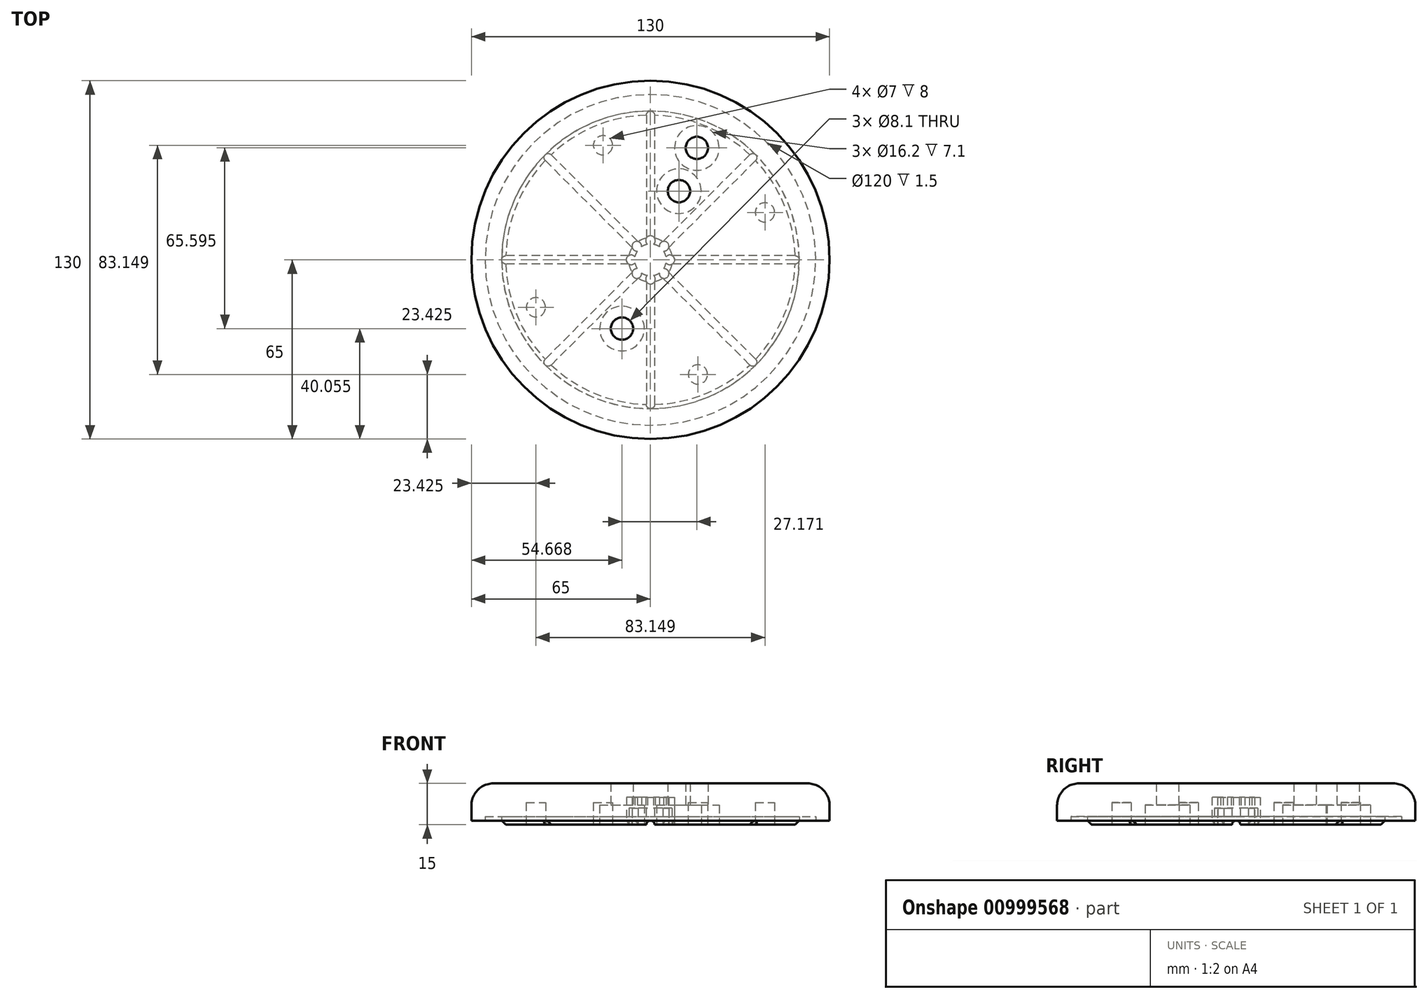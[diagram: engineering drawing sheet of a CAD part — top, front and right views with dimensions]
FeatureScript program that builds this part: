
annotation { "Feature Type Name" : "Feature", "Feature Type Description" : "" }
export const myFeature = defineFeature(function(context is Context, id is Id, definition is map)
    precondition{}
    {
        {
            var Q0;
            Q0=qCreatedBy(makeId("Top.planeOp"),FACE);
            var sketch = newSketch(context, id + "F0", { "sketchPlane" : qUnion([Q0])});
            skCircle(sketch, "E0", {"center": v(0, 0) * mm, "radius": 65 * mm});
            skSolve(sketch);
        }
        {
            var Q0;
            Q0 = qSketchRegion(id + "F0", true);
            extrude(context, id + "F1", {"entities" : qUnion([Q0]), "depth" : 15 * mm, "offsetDistance" : 25.4 * mm});
        }
        {
            var Q0;
            Q0=makeQuery(id+"F1.opExtrude","CAP_FACE",FACE,{"disambiguationData":[OSD([sQuery(id+"F0.wireOp",EDGE,"E0")])],"isStart":false});
            fillet(context, id + "F2", {"entities" : qUnion([Q0]), "radius" : 8 * mm, "tangentPropagation" : true, "allowEdgeOverflow" : false});
        }
        {
            var Q0;
            Q0=makeQuery(id+"F1.opExtrude","CAP_FACE",FACE,{"disambiguationData":[OSD([sQuery(id+"F0.wireOp",EDGE,"E0")])],"isStart":true});
            var sketch = newSketch(context, id + "F3", { "sketchPlane" : qUnion([Q0])});
            skCircle(sketch, "E1", {"center": v(0, 0) * mm, "radius": 67.5 * mm});
            skCircle(sketch, "E2", {"center": v(0, 0) * mm, "radius": 54 * mm});
            skCircle(sketch, "E3", {"center": v(0, 0) * mm, "radius": 60 * mm});
            skSolve(sketch);
        }
        {
            var Q0;
            Q0=makeQuery(id+"F3.imprint","IMPRINT",FACE,{"disambiguationData":[TD([[makeQuery(id+"F3.imprint","IMPRINT",EDGE,{"derivedFrom":sQuery(id+"F3.wireOp",EDGE,"E2")}),-1.0]])]});
            extrude(context, id + "F4", {"entities" : qUnion([Q0]), "operationType" : NewBodyOperationType.REMOVE, "oppositeDirection" : true, "depth" : 3 * mm, "offsetDistance" : 25 * mm});
        }
        {
            var Q0;
            Q0=makeQuery(id+"F1.opExtrude","CAP_FACE",FACE,{"disambiguationData":[OSD([sQuery(id+"F0.wireOp",EDGE,"E0")])],"isStart":true});
            var sketch = newSketch(context, id + "F5", { "sketchPlane" : qUnion([Q0])});
            skCircle(sketch, "E4", {"center": v(0, 0) * mm, "radius": 8 * mm});
            skSolve(sketch);
        }
        {
            var Q0;
            Q0=makeQuery(id+"F5.imprint","IMPRINT",FACE,{"disambiguationData":[TD([[makeQuery(id+"F5.imprint","IMPRINT",EDGE,{"derivedFrom":sQuery(id+"F5.wireOp",EDGE,"E4")}),1.0]])]});
            extrude(context, id + "F6", {"entities" : qUnion([Q0]), "operationType" : NewBodyOperationType.REMOVE, "oppositeDirection" : true, "depth" : 10 * mm, "offsetDistance" : 25 * mm});
        }
        {
            var Q0;
            Q0=qCreatedBy(makeId("Front.planeOp"),FACE);
            var Q1;
            Q1=qCreatedBy(makeId("Right.planeOp"),FACE);
            cPlane(context, id + "F7", {"entities" : qUnion([Q0, Q1]), "cplaneType" : CPlaneType.MID_PLANE, "offset" : 25 * mm, "width" : 150 * mm, "height" : 150 * mm});
        }
        {
            var Q0;
            Q0=qCreatedBy(makeId("Front.planeOp"),FACE);
            var Q1;
            Q1=qCreatedBy(makeId("Right.planeOp"),FACE);
            cPlane(context, id + "F8", {"entities" : qUnion([Q0, Q1]), "cplaneType" : CPlaneType.MID_PLANE, "offset" : 25 * mm, "flipAlignment" : true, "width" : 150 * mm, "height" : 150 * mm});
        }
        {
            var Q0;
            Q0=qCreatedBy(makeId("Front.planeOp"),FACE);
            var sketch = newSketch(context, id + "F9", { "sketchPlane" : qUnion([Q0])});
            skCircle(sketch, "E5", {"center": v(0, 0) * mm, "radius": 1.5 * mm});
            skSolve(sketch);
        }
        {
            var Q0;
            Q0=makeQuery(id+"F9.imprint","IMPRINT",FACE,{"disambiguationData":[TD([[makeQuery(id+"F9.imprint","IMPRINT",EDGE,{"derivedFrom":sQuery(id+"F9.wireOp",EDGE,"E5")}),1.0]])]});
            var Q1;
            Q1=makeQuery(id+"F4.boolean.opBoolean","COPY",FACE,{"derivedFrom":makeQuery(id+"F4.opExtrude","SWEPT_FACE",FACE,{"disambiguationData":[OSD([sQuery(id+"F3.wireOp",EDGE,"E2")])]})});
            var Q2;
            Q2=makeQuery(id+"F4.boolean.opBoolean","COPY",FACE,{"derivedFrom":makeQuery(id+"F4.opExtrude","SWEPT_FACE",FACE,{"disambiguationData":[OSD([sQuery(id+"F3.wireOp",EDGE,"E2")])]})});
            extrude(context, id + "F10", {"entities" : qUnion([Q0]), "operationType" : NewBodyOperationType.REMOVE, "endBound" : BoundingType.UP_TO_SURFACE, "oppositeDirection" : true, "depth" : 25 * mm, "endBoundEntityFace" : qUnion([Q1]), "offsetDistance" : 25 * mm, "hasSecondDirection" : true, "secondDirectionBound" : SecondDirectionBoundingType.UP_TO_SURFACE, "secondDirectionOppositeDirection" : false, "secondDirectionDepth" : 25 * mm, "secondDirectionBoundEntityFace" : qUnion([Q2])});
        }
        {
            var Q0;
            Q0=qCreatedBy(makeId("Right.planeOp"),FACE);
            var sketch = newSketch(context, id + "F11", { "sketchPlane" : qUnion([Q0])});
            skCircle(sketch, "E6", {"center": v(0, 0) * mm, "radius": 1.5 * mm});
            skSolve(sketch);
        }
        {
            var Q0;
            Q0=makeQuery(id+"F11.imprint","IMPRINT",FACE,{"disambiguationData":[TD([[makeQuery(id+"F11.imprint","IMPRINT",EDGE,{"derivedFrom":sQuery(id+"F11.wireOp",EDGE,"E6")}),1.0]])]});
            var Q1;
            Q1=makeQuery(id+"F4.boolean.opBoolean","COPY",FACE,{"derivedFrom":makeQuery(id+"F4.opExtrude","SWEPT_FACE",FACE,{"disambiguationData":[OSD([sQuery(id+"F3.wireOp",EDGE,"E2")])]})});
            var Q2;
            Q2=makeQuery(id+"F4.boolean.opBoolean","COPY",FACE,{"derivedFrom":makeQuery(id+"F4.opExtrude","SWEPT_FACE",FACE,{"disambiguationData":[OSD([sQuery(id+"F3.wireOp",EDGE,"E2")])]})});
            extrude(context, id + "F12", {"entities" : qUnion([Q0]), "operationType" : NewBodyOperationType.REMOVE, "endBound" : BoundingType.UP_TO_SURFACE, "depth" : 25 * mm, "endBoundEntityFace" : qUnion([Q1]), "offsetDistance" : 25 * mm, "hasSecondDirection" : true, "secondDirectionBound" : SecondDirectionBoundingType.UP_TO_SURFACE, "secondDirectionOppositeDirection" : true, "secondDirectionDepth" : 25 * mm, "secondDirectionBoundEntityFace" : qUnion([Q2])});
        }
        {
            var Q0;
            Q0=qCreatedBy(id+"F7.planeOp",FACE);
            var sketch = newSketch(context, id + "F13", { "sketchPlane" : qUnion([Q0])});
            skCircle(sketch, "E7", {"center": v(0, 0) * mm, "radius": 1.5 * mm});
            skSolve(sketch);
        }
        {
            var Q0;
            Q0 = qSketchRegion(id + "F13", true);
            var Q1;
            Q1=makeQuery(id+"F4.boolean.opBoolean","COPY",FACE,{"derivedFrom":makeQuery(id+"F4.opExtrude","SWEPT_FACE",FACE,{"disambiguationData":[OSD([sQuery(id+"F3.wireOp",EDGE,"E2")])]})});
            var Q2;
            Q2=makeQuery(id+"F4.boolean.opBoolean","COPY",FACE,{"derivedFrom":makeQuery(id+"F4.opExtrude","SWEPT_FACE",FACE,{"disambiguationData":[OSD([sQuery(id+"F3.wireOp",EDGE,"E2")])]})});
            extrude(context, id + "F14", {"entities" : qUnion([Q0]), "operationType" : NewBodyOperationType.REMOVE, "endBound" : BoundingType.UP_TO_SURFACE, "oppositeDirection" : true, "depth" : 25 * mm, "endBoundEntityFace" : qUnion([Q1]), "offsetDistance" : 25 * mm, "hasSecondDirection" : true, "secondDirectionBound" : SecondDirectionBoundingType.UP_TO_SURFACE, "secondDirectionOppositeDirection" : false, "secondDirectionDepth" : 25 * mm, "secondDirectionBoundEntityFace" : qUnion([Q2])});
        }
        {
            var Q0;
            Q0=qCreatedBy(id+"F8.planeOp",FACE);
            var sketch = newSketch(context, id + "F15", { "sketchPlane" : qUnion([Q0])});
            skCircle(sketch, "E8", {"center": v(0, 0) * mm, "radius": 1.5 * mm});
            skSolve(sketch);
        }
        {
            var Q0;
            Q0 = qSketchRegion(id + "F15", true);
            var Q1;
            Q1=makeQuery(id+"F4.boolean.opBoolean","COPY",FACE,{"derivedFrom":makeQuery(id+"F4.opExtrude","SWEPT_FACE",FACE,{"disambiguationData":[OSD([sQuery(id+"F3.wireOp",EDGE,"E2")])]})});
            var Q2;
            Q2=makeQuery(id+"F4.boolean.opBoolean","COPY",FACE,{"derivedFrom":makeQuery(id+"F4.opExtrude","SWEPT_FACE",FACE,{"disambiguationData":[OSD([sQuery(id+"F3.wireOp",EDGE,"E2")])]})});
            extrude(context, id + "F16", {"entities" : qUnion([Q0]), "operationType" : NewBodyOperationType.REMOVE, "endBound" : BoundingType.UP_TO_SURFACE, "oppositeDirection" : true, "depth" : 25 * mm, "endBoundEntityFace" : qUnion([Q1]), "offsetDistance" : 25 * mm, "hasSecondDirection" : true, "secondDirectionBound" : SecondDirectionBoundingType.UP_TO_SURFACE, "secondDirectionOppositeDirection" : false, "secondDirectionDepth" : 25 * mm, "secondDirectionBoundEntityFace" : qUnion([Q2])});
        }
        {
            var Q0;
            Q0=makeQuery(id+"F6.boolean.opBoolean","COPY",FACE,{"derivedFrom":makeQuery(id+"F6.opExtrude","CAP_FACE",FACE,{"disambiguationData":[OSD([sQuery(id+"F5.wireOp",EDGE,"E4")])],"isStart":false})});
            var sketch = newSketch(context, id + "F17", { "sketchPlane" : qUnion([Q0])});
            skCircle(sketch, "E9.0", {"center": v(0, 0) * mm, "radius": 8 * mm});
            skCircle(sketch, "E10", {"center": v(0, 0) * mm, "radius": 5.75 * mm});
            skSolve(sketch);
        }
        {
            var Q0;
            Q0=makeQuery(id+"F17.imprint","IMPRINT",FACE,{"disambiguationData":[TD([[makeQuery(id+"F17.imprint","IMPRINT",EDGE,{"derivedFrom":sQuery(id+"F17.wireOp",EDGE,"E9.0")}),1.0]])]});
            extrude(context, id + "F18", {"entities" : qUnion([Q0]), "operationType" : NewBodyOperationType.ADD, "depth" : 4 * mm, "offsetDistance" : 25 * mm});
        }
        {
            var Q0;
            Q0=makeQuery(id+"F12.boolean.opBoolean","SPLIT",FACE,{"disambiguationData":[TD([makeQuery(id+"F10.boolean.opBoolean","COPY",FACE,{"disambiguationData":[OD(0.0)],"derivedFrom":makeQuery(id+"F10.opExtrude","SWEPT_FACE",FACE,{"disambiguationData":[OSD([sQuery(id+"F9.wireOp",EDGE,"E5")])]})})])],"derivedFrom":makeQuery(id+"F10.boolean.opBoolean","SPLIT",FACE,{"disambiguationData":[OD(0.0)],"derivedFrom":makeQuery(id+"F1.opExtrude","CAP_FACE",FACE,{"disambiguationData":[OSD([sQuery(id+"F0.wireOp",EDGE,"E0")])],"isStart":true})})});
            var sketch = newSketch(context, id + "F19", { "sketchPlane" : qUnion([Q0])});
            skCircle(sketch, "E11", {"center": v(0, 7) * mm, "radius": 1.75 * mm});
            skCircle(sketch, "E12.1.0", {"center": v(-4.95, 4.95) * mm, "radius": 1.75 * mm});
            skCircle(sketch, "E12.2.0", {"center": v(-7, 0) * mm, "radius": 1.75 * mm});
            skCircle(sketch, "E12.3.0", {"center": v(-4.95, -4.95) * mm, "radius": 1.75 * mm});
            skPoint(sketch, "E12.center", {"position": v(0, 0) * mm});
            skCircle(sketch, "E13.1.4.0", {"center": v(0, -7) * mm, "radius": 1.75 * mm});
            skCircle(sketch, "E13.1.5.0", {"center": v(4.95, -4.95) * mm, "radius": 1.75 * mm});
            skCircle(sketch, "E14.1.6.0", {"center": v(7, 0) * mm, "radius": 1.75 * mm});
            skCircle(sketch, "E14.1.7.0", {"center": v(4.95, 4.95) * mm, "radius": 1.75 * mm});
            skSolve(sketch);
        }
        {
            var Q0;
            Q0 = qSketchRegion(id + "F19", true);
            extrude(context, id + "F20", {"entities" : qUnion([Q0]), "operationType" : NewBodyOperationType.REMOVE, "oppositeDirection" : true, "depth" : 10 * mm, "offsetDistance" : 25 * mm});
        }
        {
            var Q0;
            {var subQ2=makeQuery(id+"F10.boolean.opBoolean","COPY",FACE,{"disambiguationData":[OD(0.0)],"derivedFrom":makeQuery(id+"F10.opExtrude","SWEPT_FACE",FACE,{"disambiguationData":[OSD([sQuery(id+"F9.wireOp",EDGE,"E5")])]})});Q0=makeQuery(id+"F14.boolean.opBoolean","SPLIT",FACE,{"disambiguationData":[TD([subQ2])],"derivedFrom":makeQuery(id+"F12.boolean.opBoolean","SPLIT",FACE,{"disambiguationData":[TD([subQ2])],"derivedFrom":makeQuery(id+"F10.boolean.opBoolean","SPLIT",FACE,{"disambiguationData":[OD(0.0)],"derivedFrom":makeQuery(id+"F1.opExtrude","CAP_FACE",FACE,{"disambiguationData":[OSD([sQuery(id+"F0.wireOp",EDGE,"E0")])],"isStart":true})})})});}
            var sketch = newSketch(context, id + "F21", { "sketchPlane" : qUnion([Q0])});
            skLineSegment(sketch, "E15", {"start": v(-20.66, 49.89) * mm, "end": v(0, 0) * mm, "construction": true});
            skLineSegment(sketch, "E16", {"start": v(0, 0) * mm, "end": v(20.66, -49.89) * mm, "construction": true});
            skCircle(sketch, "E17", {"center": v(-10.33, 24.94) * mm, "radius": 4.05 * mm});
            skCircle(sketch, "E18", {"center": v(10.33, -24.94) * mm, "radius": 4.05 * mm});
            skCircle(sketch, "E19", {"center": v(16.84, -40.65) * mm, "radius": 4.05 * mm});
            skSolve(sketch);
        }
        {
            var Q0;
            Q0 = qSketchRegion(id + "F21", true);
            extrude(context, id + "F22", {"entities" : qUnion([Q0]), "operationType" : NewBodyOperationType.REMOVE, "endBound" : BoundingType.THROUGH_ALL, "oppositeDirection" : true, "depth" : 25 * mm, "offsetDistance" : 25 * mm});
        }
        {
            var Q0;
            {var subQ2=makeQuery(id+"F10.boolean.opBoolean","COPY",FACE,{"disambiguationData":[OD(0.0)],"derivedFrom":makeQuery(id+"F10.opExtrude","SWEPT_FACE",FACE,{"disambiguationData":[OSD([sQuery(id+"F9.wireOp",EDGE,"E5")])]})});Q0=makeQuery(id+"F14.boolean.opBoolean","SPLIT",FACE,{"disambiguationData":[TD([subQ2])],"derivedFrom":makeQuery(id+"F12.boolean.opBoolean","SPLIT",FACE,{"disambiguationData":[TD([subQ2])],"derivedFrom":makeQuery(id+"F10.boolean.opBoolean","SPLIT",FACE,{"disambiguationData":[OD(0.0)],"derivedFrom":makeQuery(id+"F1.opExtrude","CAP_FACE",FACE,{"disambiguationData":[OSD([sQuery(id+"F0.wireOp",EDGE,"E0")])],"isStart":true})})})});}
            var sketch = newSketch(context, id + "F23", { "sketchPlane" : qUnion([Q0])});
            skCircle(sketch, "E20", {"center": v(-10.33, 24.94) * mm, "radius": 8.1 * mm});
            skCircle(sketch, "E21", {"center": v(10.33, -24.94) * mm, "radius": 8.1 * mm});
            skCircle(sketch, "E22", {"center": v(16.84, -40.65) * mm, "radius": 8.1 * mm});
            skSolve(sketch);
        }
        {
            var Q0;
            Q0 = qSketchRegion(id + "F23", true);
            extrude(context, id + "F24", {"entities" : qUnion([Q0]), "operationType" : NewBodyOperationType.REMOVE, "oppositeDirection" : true, "depth" : 7.1 * mm, "offsetDistance" : 25 * mm});
        }
        {
            var Q0;
            {var subQ2=makeQuery(id+"F12.opExtrude","SWEPT_FACE",FACE,{"disambiguationData":[OSD([sQuery(id+"F11.wireOp",EDGE,"E6")])]});Q0=makeQuery(id+"F14.boolean.opBoolean","SPLIT",FACE,{"disambiguationData":[TD([makeQuery(id+"F12.boolean.opBoolean","COPY",FACE,{"disambiguationData":[OD(0.0)],"derivedFrom":subQ2})])],"derivedFrom":makeQuery(id+"F12.boolean.opBoolean","SPLIT",FACE,{"disambiguationData":[TD([makeQuery(id+"F10.boolean.opBoolean","COPY",FACE,{"disambiguationData":[OD(0.0)],"derivedFrom":makeQuery(id+"F10.opExtrude","SWEPT_FACE",FACE,{"disambiguationData":[OSD([sQuery(id+"F9.wireOp",EDGE,"E5")])]})})])],"derivedFrom":makeQuery(id+"F10.boolean.opBoolean","SPLIT",FACE,{"disambiguationData":[OD(0.0)],"derivedFrom":makeQuery(id+"F1.opExtrude","CAP_FACE",FACE,{"disambiguationData":[OSD([sQuery(id+"F0.wireOp",EDGE,"E0")])],"isStart":true})})})});}
            var sketch = newSketch(context, id + "F25", { "sketchPlane" : qUnion([Q0])});
            skCircle(sketch, "E23", {"center": v(-41.57, 17.22) * mm, "radius": 3.5 * mm});
            skLineSegment(sketch, "E24", {"start": v(0, 0) * mm, "end": v(-57.74, 23.92) * mm, "construction": true});
            skPoint(sketch, "E25.center", {"position": v(9.24, -3.83) * mm});
            skCircle(sketch, "E26.1.0", {"center": v(-17.22, -41.57) * mm, "radius": 3.5 * mm});
            skCircle(sketch, "E26.2.0", {"center": v(41.57, -17.22) * mm, "radius": 3.5 * mm});
            skCircle(sketch, "E26.3.0", {"center": v(17.22, 41.57) * mm, "radius": 3.5 * mm});
            skPoint(sketch, "E26.center", {"position": v(0, 0) * mm});
            skSolve(sketch);
        }
        {
            var Q0;
            Q0 = qSketchRegion(id + "F25", true);
            extrude(context, id + "F26", {"entities" : qUnion([Q0]), "operationType" : NewBodyOperationType.REMOVE, "oppositeDirection" : true, "depth" : 8 * mm, "offsetDistance" : 25 * mm});
        }
        {
            var Q0;
            {var subQ0=sQuery(id+"F0.wireOp",EDGE,"E0");Q0=makeQuery(id+"F4.boolean.opBoolean","SPLIT",FACE,{"disambiguationData":[TD([makeQuery(id+"F1.opExtrude","SWEPT_FACE",FACE,{"disambiguationData":[OSD([subQ0])]})])],"derivedFrom":makeQuery(id+"F1.opExtrude","CAP_FACE",FACE,{"disambiguationData":[OSD([subQ0])],"isStart":true})});}
            var sketch = newSketch(context, id + "F27", { "sketchPlane" : qUnion([Q0])});
            skCircle(sketch, "E27.0", {"center": v(0, 0) * mm, "radius": 65 * mm});
            skCircle(sketch, "E28.0", {"center": v(0, 0) * mm, "radius": 60 * mm});
            skSolve(sketch);
        }
        {
            var Q0;
            Q0 = qSketchRegion(id + "F27", true);
            extrude(context, id + "F28", {"entities" : qUnion([Q0]), "operationType" : NewBodyOperationType.REMOVE, "oppositeDirection" : true, "depth" : 1.5 * mm, "offsetDistance" : 25 * mm});
        }
        {
            var Q0;
            {var subQ1=sQuery(id+"F3.wireOp",EDGE,"E2");var subQ3=makeQuery(id+"F10.boolean.opBoolean","COPY",FACE,{"disambiguationData":[OD(0.0)],"derivedFrom":makeQuery(id+"F10.opExtrude","SWEPT_FACE",FACE,{"disambiguationData":[OSD([sQuery(id+"F9.wireOp",EDGE,"E5")])]})});Q0=makeQuery(id+"F14.boolean.opBoolean","SPLIT",EDGE,{"disambiguationData":[TD([subQ3])],"derivedFrom":makeQuery(id+"F12.boolean.opBoolean","SPLIT",EDGE,{"disambiguationData":[TD([subQ3])],"derivedFrom":makeQuery(id+"F10.boolean.opBoolean","SPLIT",EDGE,{"disambiguationData":[OD(0.0)],"derivedFrom":makeQuery(id+"F4.boolean.opBoolean","COPY",EDGE,{"derivedFrom":makeQuery(id+"F4.opExtrude","CAP_EDGE",EDGE,{"disambiguationData":[OSD([subQ1])],"isStart":true})})})})});}
            var Q1;
            {var subQ1=sQuery(id+"F3.wireOp",EDGE,"E2");var subQ3=makeQuery(id+"F10.boolean.opBoolean","COPY",FACE,{"disambiguationData":[OD(0.0)],"derivedFrom":makeQuery(id+"F10.opExtrude","SWEPT_FACE",FACE,{"disambiguationData":[OSD([sQuery(id+"F9.wireOp",EDGE,"E5")])]})});Q1=makeQuery(id+"F16.boolean.opBoolean","SPLIT",EDGE,{"disambiguationData":[TD([subQ3])],"derivedFrom":makeQuery(id+"F12.boolean.opBoolean","SPLIT",EDGE,{"disambiguationData":[TD([subQ3])],"derivedFrom":makeQuery(id+"F10.boolean.opBoolean","SPLIT",EDGE,{"disambiguationData":[OD(1.0)],"derivedFrom":makeQuery(id+"F4.boolean.opBoolean","COPY",EDGE,{"derivedFrom":makeQuery(id+"F4.opExtrude","CAP_EDGE",EDGE,{"disambiguationData":[OSD([subQ1])],"isStart":true})})})})});}
            var Q2;
            {var subQ1=makeQuery(id+"F12.opExtrude","SWEPT_FACE",FACE,{"disambiguationData":[OSD([sQuery(id+"F11.wireOp",EDGE,"E6")])]});var subQ2=sQuery(id+"F3.wireOp",EDGE,"E2");Q2=makeQuery(id+"F16.boolean.opBoolean","SPLIT",EDGE,{"disambiguationData":[TD([makeQuery(id+"F12.boolean.opBoolean","COPY",FACE,{"disambiguationData":[OD(1.0)],"derivedFrom":subQ1})])],"derivedFrom":makeQuery(id+"F12.boolean.opBoolean","SPLIT",EDGE,{"disambiguationData":[TD([makeQuery(id+"F10.boolean.opBoolean","COPY",FACE,{"disambiguationData":[OD(0.0)],"derivedFrom":makeQuery(id+"F10.opExtrude","SWEPT_FACE",FACE,{"disambiguationData":[OSD([sQuery(id+"F9.wireOp",EDGE,"E5")])]})})])],"derivedFrom":makeQuery(id+"F10.boolean.opBoolean","SPLIT",EDGE,{"disambiguationData":[OD(1.0)],"derivedFrom":makeQuery(id+"F4.boolean.opBoolean","COPY",EDGE,{"derivedFrom":makeQuery(id+"F4.opExtrude","CAP_EDGE",EDGE,{"disambiguationData":[OSD([subQ2])],"isStart":true})})})})});}
            var Q3;
            {var subQ1=makeQuery(id+"F12.opExtrude","SWEPT_FACE",FACE,{"disambiguationData":[OSD([sQuery(id+"F11.wireOp",EDGE,"E6")])]});var subQ2=sQuery(id+"F3.wireOp",EDGE,"E2");Q3=makeQuery(id+"F14.boolean.opBoolean","SPLIT",EDGE,{"disambiguationData":[TD([makeQuery(id+"F12.boolean.opBoolean","COPY",FACE,{"disambiguationData":[OD(1.0)],"derivedFrom":subQ1})])],"derivedFrom":makeQuery(id+"F12.boolean.opBoolean","SPLIT",EDGE,{"disambiguationData":[TD([makeQuery(id+"F10.boolean.opBoolean","COPY",FACE,{"disambiguationData":[OD(1.0)],"derivedFrom":makeQuery(id+"F10.opExtrude","SWEPT_FACE",FACE,{"disambiguationData":[OSD([sQuery(id+"F9.wireOp",EDGE,"E5")])]})})])],"derivedFrom":makeQuery(id+"F10.boolean.opBoolean","SPLIT",EDGE,{"disambiguationData":[OD(1.0)],"derivedFrom":makeQuery(id+"F4.boolean.opBoolean","COPY",EDGE,{"derivedFrom":makeQuery(id+"F4.opExtrude","CAP_EDGE",EDGE,{"disambiguationData":[OSD([subQ2])],"isStart":true})})})})});}
            var Q4;
            {var subQ1=sQuery(id+"F3.wireOp",EDGE,"E2");var subQ3=makeQuery(id+"F12.opExtrude","SWEPT_FACE",FACE,{"disambiguationData":[OSD([sQuery(id+"F11.wireOp",EDGE,"E6")])]});Q4=makeQuery(id+"F14.boolean.opBoolean","SPLIT",EDGE,{"disambiguationData":[TD([makeQuery(id+"F12.boolean.opBoolean","COPY",FACE,{"disambiguationData":[OD(0.0)],"derivedFrom":subQ3})])],"derivedFrom":makeQuery(id+"F12.boolean.opBoolean","SPLIT",EDGE,{"disambiguationData":[TD([makeQuery(id+"F10.boolean.opBoolean","COPY",FACE,{"disambiguationData":[OD(0.0)],"derivedFrom":makeQuery(id+"F10.opExtrude","SWEPT_FACE",FACE,{"disambiguationData":[OSD([sQuery(id+"F9.wireOp",EDGE,"E5")])]})})])],"derivedFrom":makeQuery(id+"F10.boolean.opBoolean","SPLIT",EDGE,{"disambiguationData":[OD(0.0)],"derivedFrom":makeQuery(id+"F4.boolean.opBoolean","COPY",EDGE,{"derivedFrom":makeQuery(id+"F4.opExtrude","CAP_EDGE",EDGE,{"disambiguationData":[OSD([subQ1])],"isStart":true})})})})});}
            var Q5;
            {var subQ1=sQuery(id+"F3.wireOp",EDGE,"E2");var subQ3=makeQuery(id+"F12.opExtrude","SWEPT_FACE",FACE,{"disambiguationData":[OSD([sQuery(id+"F11.wireOp",EDGE,"E6")])]});Q5=makeQuery(id+"F16.boolean.opBoolean","SPLIT",EDGE,{"disambiguationData":[TD([makeQuery(id+"F12.boolean.opBoolean","COPY",FACE,{"disambiguationData":[OD(0.0)],"derivedFrom":subQ3})])],"derivedFrom":makeQuery(id+"F12.boolean.opBoolean","SPLIT",EDGE,{"disambiguationData":[TD([makeQuery(id+"F10.boolean.opBoolean","COPY",FACE,{"disambiguationData":[OD(1.0)],"derivedFrom":makeQuery(id+"F10.opExtrude","SWEPT_FACE",FACE,{"disambiguationData":[OSD([sQuery(id+"F9.wireOp",EDGE,"E5")])]})})])],"derivedFrom":makeQuery(id+"F10.boolean.opBoolean","SPLIT",EDGE,{"disambiguationData":[OD(0.0)],"derivedFrom":makeQuery(id+"F4.boolean.opBoolean","COPY",EDGE,{"derivedFrom":makeQuery(id+"F4.opExtrude","CAP_EDGE",EDGE,{"disambiguationData":[OSD([subQ1])],"isStart":true})})})})});}
            var Q6;
            {var subQ1=sQuery(id+"F3.wireOp",EDGE,"E2");var subQ3=makeQuery(id+"F10.boolean.opBoolean","COPY",FACE,{"disambiguationData":[OD(1.0)],"derivedFrom":makeQuery(id+"F10.opExtrude","SWEPT_FACE",FACE,{"disambiguationData":[OSD([sQuery(id+"F9.wireOp",EDGE,"E5")])]})});Q6=makeQuery(id+"F16.boolean.opBoolean","SPLIT",EDGE,{"disambiguationData":[TD([subQ3])],"derivedFrom":makeQuery(id+"F12.boolean.opBoolean","SPLIT",EDGE,{"disambiguationData":[TD([subQ3])],"derivedFrom":makeQuery(id+"F10.boolean.opBoolean","SPLIT",EDGE,{"disambiguationData":[OD(0.0)],"derivedFrom":makeQuery(id+"F4.boolean.opBoolean","COPY",EDGE,{"derivedFrom":makeQuery(id+"F4.opExtrude","CAP_EDGE",EDGE,{"disambiguationData":[OSD([subQ1])],"isStart":true})})})})});}
            var Q7;
            {var subQ1=sQuery(id+"F3.wireOp",EDGE,"E2");var subQ3=makeQuery(id+"F10.boolean.opBoolean","COPY",FACE,{"disambiguationData":[OD(1.0)],"derivedFrom":makeQuery(id+"F10.opExtrude","SWEPT_FACE",FACE,{"disambiguationData":[OSD([sQuery(id+"F9.wireOp",EDGE,"E5")])]})});Q7=makeQuery(id+"F14.boolean.opBoolean","SPLIT",EDGE,{"disambiguationData":[TD([subQ3])],"derivedFrom":makeQuery(id+"F12.boolean.opBoolean","SPLIT",EDGE,{"disambiguationData":[TD([subQ3])],"derivedFrom":makeQuery(id+"F10.boolean.opBoolean","SPLIT",EDGE,{"disambiguationData":[OD(1.0)],"derivedFrom":makeQuery(id+"F4.boolean.opBoolean","COPY",EDGE,{"derivedFrom":makeQuery(id+"F4.opExtrude","CAP_EDGE",EDGE,{"disambiguationData":[OSD([subQ1])],"isStart":true})})})})});}
            chamfer(context, id + "F29", {"entities" : qUnion([Q0, Q1, Q2, Q3, Q4, Q5, Q6, Q7]), "width" : 1.5 * mm, "tangentPropagation" : true});
        }
    });
